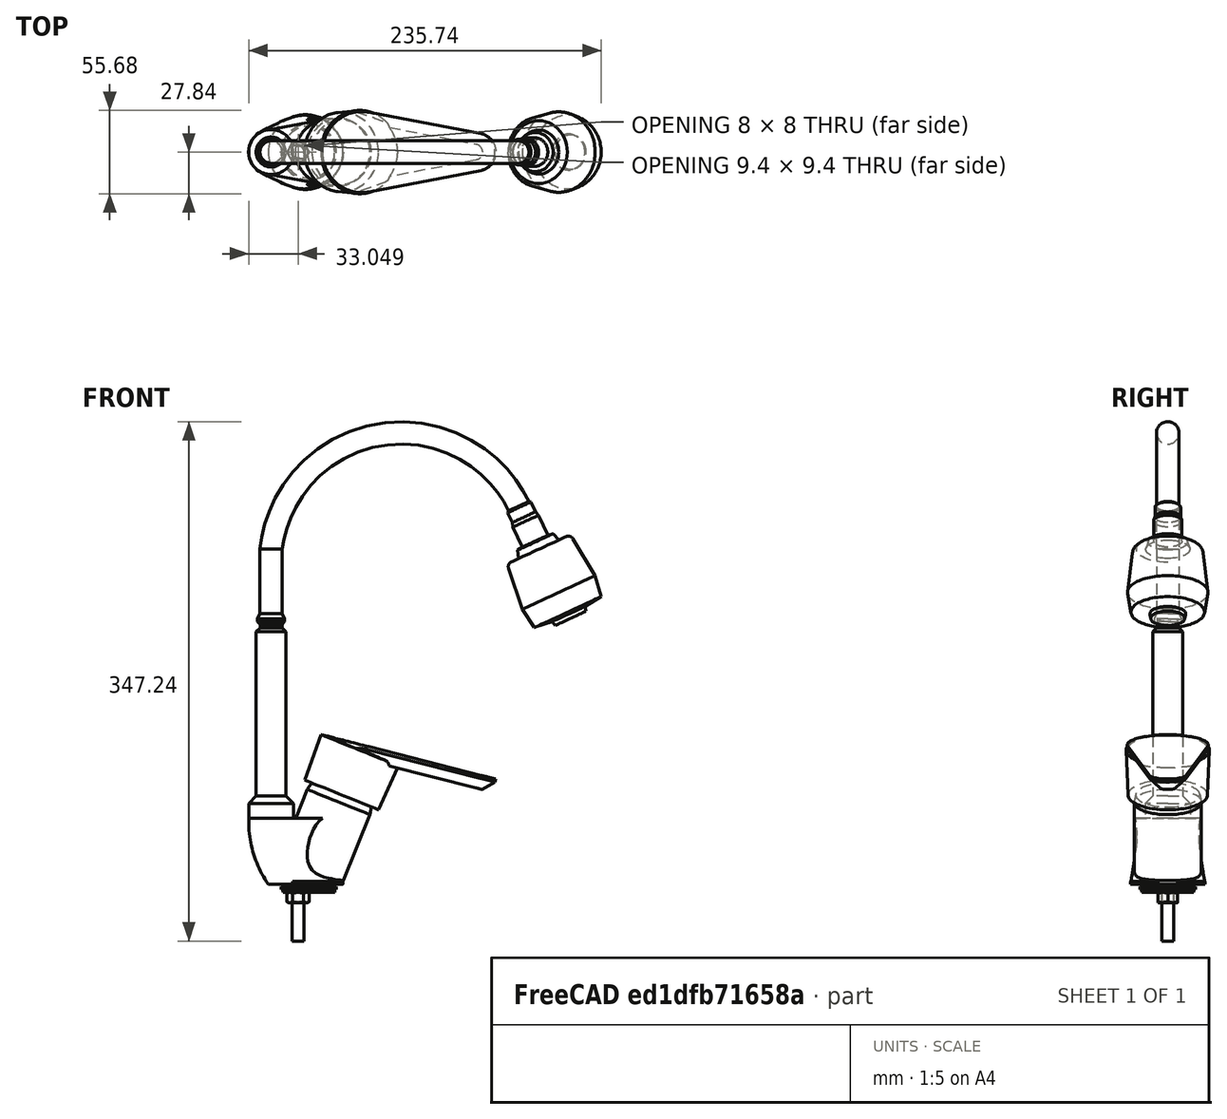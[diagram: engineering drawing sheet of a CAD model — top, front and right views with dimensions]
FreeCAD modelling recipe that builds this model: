
FCSTD DOCUMENT  (FreeCAD 1.0R38641 +468 (Git))
Label: Faucet_Solone LOP4-B043-21
License: All rights reserved
objects: Part::Feature×1, Part::FeaturePython×1
note: 2 computed .brp shape members not serialized (recipe doc carries the construction recipe); baked Part::Feature solids carry a one-line shape summary decoded from their .brp

FEATURE [Part::Feature] Compound  label="c LOP4-B043-21"
  Placement = pos=(0,0,0) rot=(-0.57735,0.57735,0.57735;4.18879rad)
  shape: bbox 236 x 55.69 x 400.4 mm, 110 faces, 2 solids (baked)
FEATURE [Part::FeaturePython] Component  label="Faucet_Solone LOP4-B043-21"  # Arch/BIM 22 (typed FeaturePython)
  Base = -> Compound
  HorizontalArea = 0
  IfcData = attributes={"GlobalId": {"name": "GlobalId", "type": "IfcGloballyUniqueId", "is_enum": false, "enum_values": []}, "Description": {"... (+538 chars omitted),+1 more (map truncated)
  IfcType = 22
  MoveBase = false
  MoveWithHost = false
  PerimeterLength = 0
  Placement = pos=(0,0,0) rot=(-0.57735,0.57735,0.57735;4.18879rad)
  VerticalArea = 0
